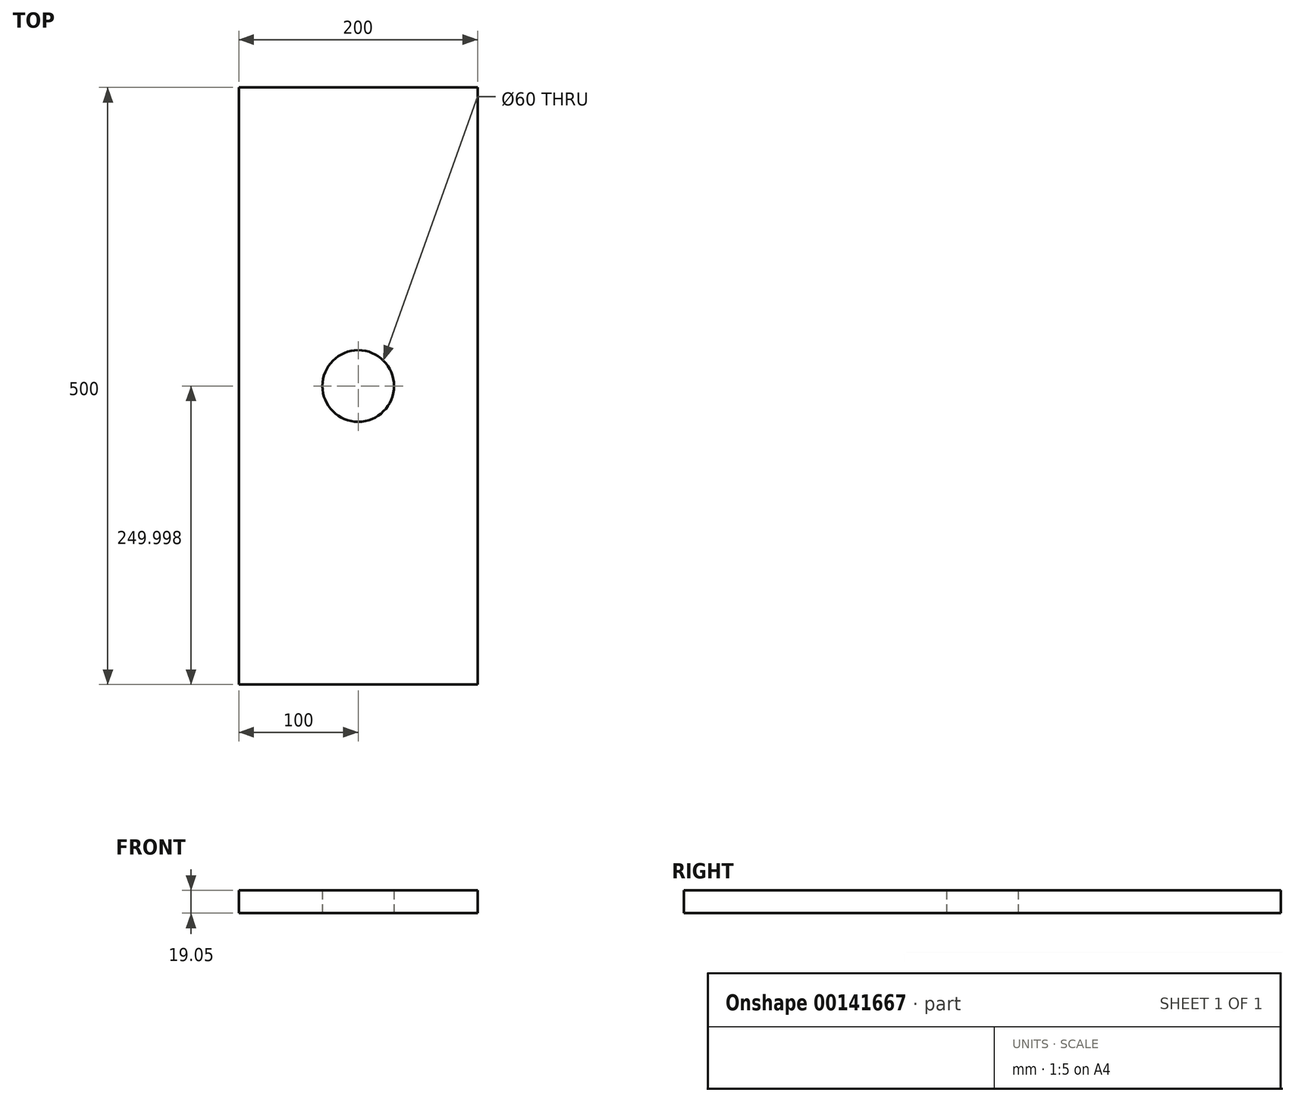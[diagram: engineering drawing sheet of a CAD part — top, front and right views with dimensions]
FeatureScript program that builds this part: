
annotation { "Feature Type Name" : "Feature", "Feature Type Description" : "" }
export const myFeature = defineFeature(function(context is Context, id is Id, definition is map)
    precondition{}
    {
        {
            var Q0;
            Q0=qCreatedBy(makeId("Top.planeOp"),FACE);
            var sketch = newSketch(context, id + "F0", { "sketchPlane" : qUnion([Q0])});
            skLineSegment(sketch, "E0", {"start": v(-373.63, -101.83) * mm, "end": v(-373.63, 398.17) * mm});
            skLineSegment(sketch, "E1", {"start": v(-373.63, 398.17) * mm, "end": v(-173.63, 398.17) * mm});
            skLineSegment(sketch, "E2", {"start": v(-173.63, 398.17) * mm, "end": v(-173.63, -101.83) * mm});
            skLineSegment(sketch, "E3", {"start": v(-173.63, -101.83) * mm, "end": v(-373.63, -101.83) * mm});
            skCircle(sketch, "E4", {"center": v(-273.63, 148.17) * mm, "radius": 30 * mm});
            skSolve(sketch);
        }
        {
            var Q0;
            Q0 = qSketchRegion(id + "F0", true);
            extrude(context, id + "F1", {"entities" : qUnion([Q0]), "depth" : 19.05 * mm});
        }
    });
